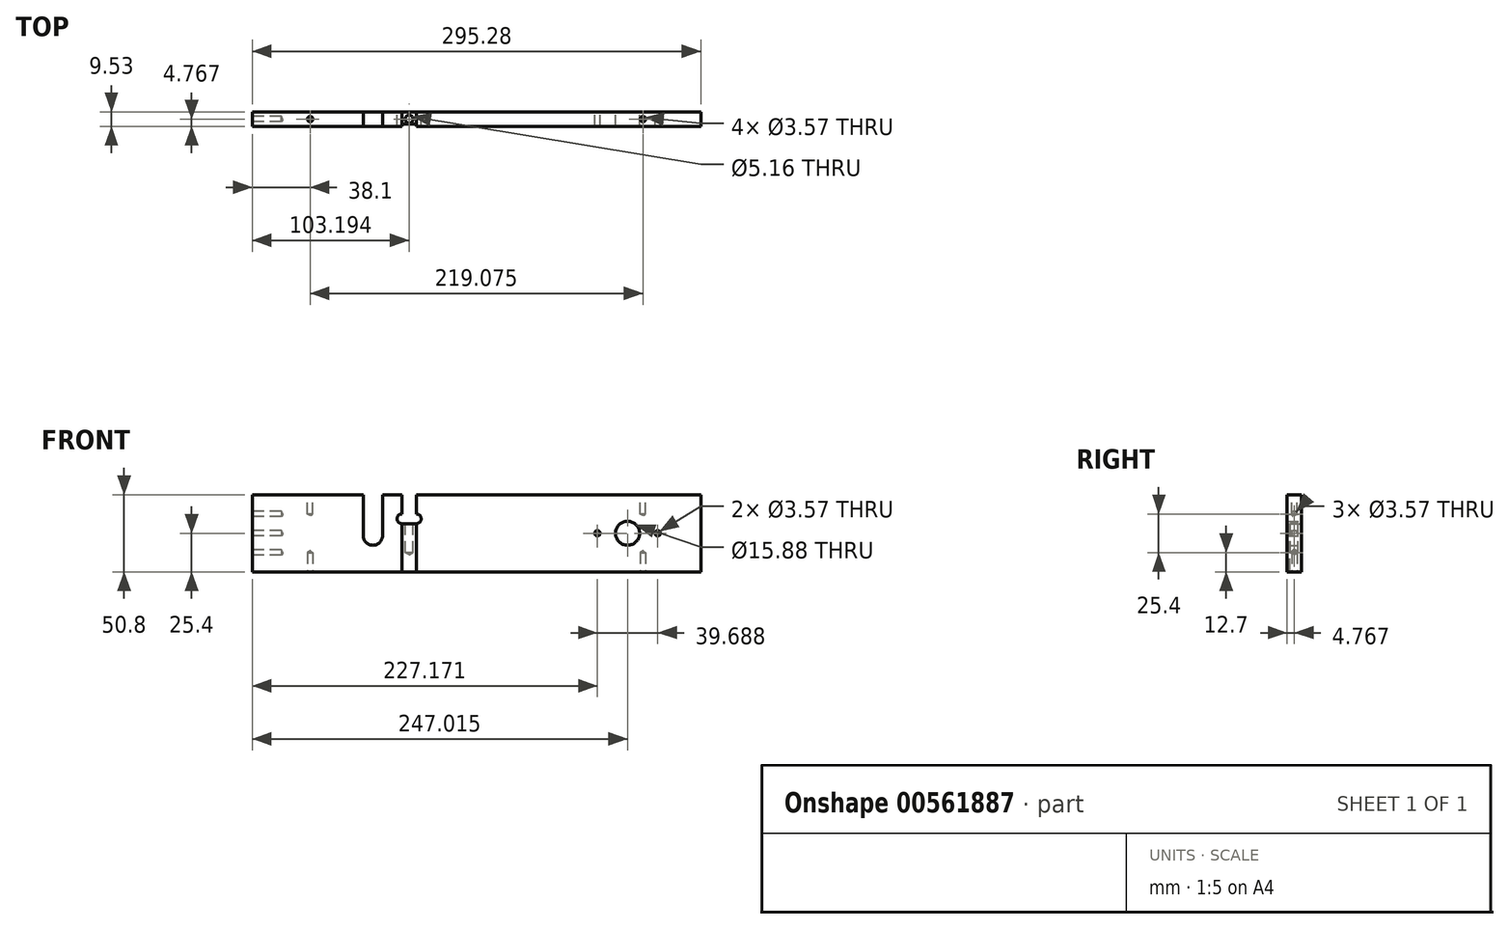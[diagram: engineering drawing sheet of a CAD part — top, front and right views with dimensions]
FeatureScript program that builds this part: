
annotation { "Feature Type Name" : "Feature", "Feature Type Description" : "" }
export const myFeature = defineFeature(function(context is Context, id is Id, definition is map)
    precondition{}
    {
        {
            var Q0;
            Q0=qCreatedBy(makeId("Front.planeOp"),FACE);
            var sketch = newSketch(context, id + "F0", { "sketchPlane" : qUnion([Q0])});
            skLineSegment(sketch, "E0", {"start": v(0, 0) * mm, "end": v(295.28, 0) * mm});
            skLineSegment(sketch, "E1", {"start": v(295.28, 0) * mm, "end": v(295.28, 50.8) * mm});
            skLineSegment(sketch, "E2", {"start": v(0, 50.8) * mm, "end": v(0, 0) * mm});
            skLineSegment(sketch, "E3", {"start": v(0, 50.8) * mm, "end": v(98.43, 50.8) * mm});
            skLineSegment(sketch, "E4", {"start": v(98.43, 50.8) * mm, "end": v(98.43, 31.75) * mm});
            skLineSegment(sketch, "E5", {"start": v(107.96, 50.8) * mm, "end": v(107.96, 31.75) * mm});
            skLineSegment(sketch, "E6", {"start": v(98.43, 31.75) * mm, "end": v(107.96, 31.75) * mm});
            skLineSegment(sketch, "E7", {"start": v(107.96, 50.8) * mm, "end": v(295.28, 50.8) * mm});
            skLineSegment(sketch, "E8", {"start": v(79.38, 50.8) * mm, "end": v(79.38, 0) * mm, "construction": true});
            skArc(sketch, "E9", {"start": v(98.42, 38.1) * mm, "mid": v(95.25, 34.92) * mm, "end": v(98.43, 31.75) * mm});
            skArc(sketch, "E10", {"start": v(107.96, 31.75) * mm, "mid": v(111.14, 34.92) * mm, "end": v(107.96, 38.1) * mm});
            skCircle(sketch, "E11", {"center": v(79.38, 25.4) * mm, "radius": 38.1 * mm, "construction": true});
            skCircle(sketch, "E12", {"center": v(79.38, 23.81) * mm, "radius": 6.35 * mm});
            skLineSegment(sketch, "E13", {"start": v(73.03, 50.8) * mm, "end": v(73.03, 23.81) * mm});
            skLineSegment(sketch, "E14", {"start": v(85.72, 50.8) * mm, "end": v(85.72, 23.81) * mm});
            skCircle(sketch, "E15", {"center": v(247.02, 25.4) * mm, "radius": 38.1 * mm, "construction": true});
            skCircle(sketch, "E16", {"center": v(247.02, 25.4) * mm, "radius": 7.94 * mm});
            skLineSegment(sketch, "E17", {"start": v(247.02, 50.8) * mm, "end": v(247.02, 0) * mm, "construction": true});
            skCircle(sketch, "E18", {"center": v(227.17, 25.4) * mm, "radius": 1.79 * mm});
            skCircle(sketch, "E19", {"center": v(266.86, 25.4) * mm, "radius": 1.79 * mm});
            skLineSegment(sketch, "E20", {"start": v(227.17, 25.4) * mm, "end": v(247.02, 25.4) * mm, "construction": true});
            skLineSegment(sketch, "E21", {"start": v(266.86, 25.4) * mm, "end": v(247.02, 25.4) * mm, "construction": true});
            skSolve(sketch);
        }
        {
            var Q0;
            Q0=makeQuery(id+"F0.imprint","IMPRINT",FACE,{"disambiguationData":[TD([[makeQuery(id+"F0.imprint","IMPRINT",EDGE,{"derivedFrom":sQuery(id+"F0.wireOp",EDGE,"E0")}),1.0]])]});
            extrude(context, id + "F1", {"entities" : qUnion([Q0]), "depth" : 9.52 * mm, "offsetDistance" : 25.4 * mm});
        }
        {
            var Q0;
            Q0=makeQuery(id+"F1.opExtrude","CAP_FACE",FACE,{"disambiguationData":[OSD([sQuery(id+"F0.wireOp",EDGE,"E0"),sQuery(id+"F0.wireOp",EDGE,"E1"),sQuery(id+"F0.wireOp",EDGE,"E2"),sQuery(id+"F0.wireOp",EDGE,"E3"),sQuery(id+"F0.wireOp",EDGE,"E4"),sQuery(id+"F0.wireOp",EDGE,"E5"),sQuery(id+"F0.wireOp",EDGE,"E6"),sQuery(id+"F0.wireOp",EDGE,"E7")])],"isStart":false});
            var sketch = newSketch(context, id + "F2", { "sketchPlane" : qUnion([Q0])});
            skLineSegment(sketch, "E22.bottom", {"start": v(107.96, 31.75) * mm, "end": v(98.43, 31.75) * mm});
            skLineSegment(sketch, "E22.top", {"start": v(107.96, 0) * mm, "end": v(98.43, 0) * mm});
            skLineSegment(sketch, "E22.left", {"start": v(107.96, 31.75) * mm, "end": v(107.96, 0) * mm});
            skLineSegment(sketch, "E22.right", {"start": v(98.43, 31.75) * mm, "end": v(98.43, 0) * mm});
            skSolve(sketch);
        }
        {
            var Q0;
            Q0=makeQuery(id+"F2.imprint","IMPRINT",FACE,{"disambiguationData":[TD([[makeQuery(id+"F2.imprint","IMPRINT",EDGE,{"derivedFrom":sQuery(id+"F2.wireOp",EDGE,"E22.bottom")}),-1.0]])]});
            extrude(context, id + "F3", {"entities" : qUnion([Q0]), "operationType" : NewBodyOperationType.REMOVE, "oppositeDirection" : true, "depth" : 1.59 * mm, "offsetDistance" : 25.4 * mm});
        }
        {
            var Q0;
            Q0=makeQuery(id+"F1.opExtrude","SWEPT_FACE",FACE,{"disambiguationData":[OSD([sQuery(id+"F0.wireOp",EDGE,"E2")])]});
            var sketch = newSketch(context, id + "F4", { "sketchPlane" : qUnion([Q0])});
            skLineSegment(sketch, "E23", {"start": v(4.76, 50.8) * mm, "end": v(4.76, 0) * mm, "construction": true});
            skLineSegment(sketch, "E24", {"start": v(0, 25.4) * mm, "end": v(9.53, 25.4) * mm, "construction": true});
            skPoint(sketch, "E25", {"position": v(4.76, 25.4) * mm});
            skPoint(sketch, "E26", {"position": v(4.76, 38.1) * mm});
            skPoint(sketch, "E27", {"position": v(4.76, 12.7) * mm});
            skSolve(sketch);
        }
        {
            var Q0;
            Q0=sQuery(id+"F4.wireOp",VERTEX,"E26");
            var Q1;
            Q1=sQuery(id+"F4.wireOp",VERTEX,"E25");
            var Q2;
            Q2=sQuery(id+"F4.wireOp",VERTEX,"E27");
            var Q3;
            Q3=makeQuery(id+"F1.opExtrude","SWEPT_BODY",BODY,{"disambiguationData":[OSD([sQuery(id+"F0.wireOp",EDGE,"E0"),sQuery(id+"F0.wireOp",EDGE,"E1"),sQuery(id+"F0.wireOp",EDGE,"E2"),sQuery(id+"F0.wireOp",EDGE,"E3"),sQuery(id+"F0.wireOp",EDGE,"E4"),sQuery(id+"F0.wireOp",EDGE,"E5"),sQuery(id+"F0.wireOp",EDGE,"E6"),sQuery(id+"F0.wireOp",EDGE,"E7"),sQuery(id+"F0.wireOp",EDGE,"E9"),sQuery(id+"F0.wireOp",EDGE,"E10"),sQuery(id+"F0.wireOp",EDGE,"E12"),sQuery(id+"F0.wireOp",EDGE,"E13"),sQuery(id+"F0.wireOp",EDGE,"E14"),sQuery(id+"F0.wireOp",EDGE,"E16")])]});
            hole(context, id + "F5", {"style" : HoleStyle.SIMPLE, "endStyle" : HoleEndStyle.BLIND, "holeDiameter" : 3.57 * mm, "majorDiameter" : 6.35 * mm, "holeDepth" : 19.05 * mm, "isTappedThrough" : true, "tappedDepth" : 12.7 * mm, "tapClearance" : 3, "startFromSketch" : true, "locations" : qUnion([Q0, Q1, Q2]), "scope" : qUnion([Q3])});
        }
        {
            var Q0;
            Q0=makeQuery(id+"F1.opExtrude","SWEPT_FACE",FACE,{"disambiguationData":[OSD([sQuery(id+"F0.wireOp",EDGE,"E6")])]});
            var sketch = newSketch(context, id + "F6", { "sketchPlane" : qUnion([Q0])});
            skLineSegment(sketch, "E28.bottom", {"start": v(98.43, 0) * mm, "end": v(107.96, 0) * mm, "construction": true});
            skLineSegment(sketch, "E28.top", {"start": v(98.43, -9.52) * mm, "end": v(107.96, -9.52) * mm, "construction": true});
            skLineSegment(sketch, "E28.left", {"start": v(98.43, 0) * mm, "end": v(98.43, -9.53) * mm, "construction": true});
            skLineSegment(sketch, "E28.right", {"start": v(107.96, 0) * mm, "end": v(107.96, -9.53) * mm, "construction": true});
            skLineSegment(sketch, "E29", {"start": v(98.43, -9.52) * mm, "end": v(107.96, 0) * mm, "construction": true});
            skLineSegment(sketch, "E30", {"start": v(98.43, 0) * mm, "end": v(107.96, -9.53) * mm, "construction": true});
            skPoint(sketch, "E31", {"position": v(103.2, -4.76) * mm});
            skSolve(sketch);
        }
        {
            var Q0;
            Q0=sQuery(id+"F6.wireOp",VERTEX,"E31");
            var Q1;
            Q1=makeQuery(id+"F1.opExtrude","SWEPT_BODY",BODY,{"disambiguationData":[OSD([sQuery(id+"F0.wireOp",EDGE,"E0"),sQuery(id+"F0.wireOp",EDGE,"E1"),sQuery(id+"F0.wireOp",EDGE,"E2"),sQuery(id+"F0.wireOp",EDGE,"E3"),sQuery(id+"F0.wireOp",EDGE,"E4"),sQuery(id+"F0.wireOp",EDGE,"E5"),sQuery(id+"F0.wireOp",EDGE,"E6"),sQuery(id+"F0.wireOp",EDGE,"E7"),sQuery(id+"F0.wireOp",EDGE,"E9"),sQuery(id+"F0.wireOp",EDGE,"E10"),sQuery(id+"F0.wireOp",EDGE,"E12"),sQuery(id+"F0.wireOp",EDGE,"E13"),sQuery(id+"F0.wireOp",EDGE,"E14"),sQuery(id+"F0.wireOp",EDGE,"E16")])]});
            hole(context, id + "F7", {"style" : HoleStyle.SIMPLE, "endStyle" : HoleEndStyle.BLIND, "holeDiameter" : 5.16 * mm, "majorDiameter" : 6.35 * mm, "holeDepth" : 19.05 * mm, "isTappedThrough" : true, "tappedDepth" : 12.7 * mm, "tapClearance" : 3, "startFromSketch" : true, "locations" : qUnion([Q0]), "scope" : qUnion([Q1])});
        }
        {
            var Q0;
            {var subQ0=sQuery(id+"F0.wireOp",EDGE,"E3");Q0=makeQuery(id+"F1.opExtrude","SWEPT_FACE",FACE,{"disambiguationData":[OSD([subQ0]),TDD([makeQuery(id+"F0.imprint","IMPRINT",EDGE,{"disambiguationData":[TD([[makeQuery(id+"F0.imprint","INTERSECT",VERTEX,{"derivedFrom":[sQuery(id+"F0.wireOp",EDGE,"E2"),subQ0]}),-1.0]])],"derivedFrom":subQ0})])]});}
            var sketch = newSketch(context, id + "F8", { "sketchPlane" : qUnion([Q0])});
            skLineSegment(sketch, "E32", {"start": v(0, -4.76) * mm, "end": v(38.1, -4.76) * mm, "construction": true});
            skPoint(sketch, "E33", {"position": v(38.1, -4.76) * mm});
            skSolve(sketch);
        }
        {
            var Q0;
            Q0=makeQuery(id+"F1.opExtrude","SWEPT_FACE",FACE,{"disambiguationData":[OSD([sQuery(id+"F0.wireOp",EDGE,"E7")])]});
            var sketch = newSketch(context, id + "F9", { "sketchPlane" : qUnion([Q0])});
            skLineSegment(sketch, "E34", {"start": v(295.28, -4.76) * mm, "end": v(257.18, -4.76) * mm, "construction": true});
            skPoint(sketch, "E35", {"position": v(257.18, -4.76) * mm});
            skSolve(sketch);
        }
        {
            var Q0;
            Q0=makeQuery(id+"F1.opExtrude","SWEPT_FACE",FACE,{"disambiguationData":[OSD([sQuery(id+"F0.wireOp",EDGE,"E0")])]});
            var sketch = newSketch(context, id + "F10", { "sketchPlane" : qUnion([Q0])});
            skLineSegment(sketch, "E36", {"start": v(0, 4.76) * mm, "end": v(38.1, 4.76) * mm, "construction": true});
            skLineSegment(sketch, "E37", {"start": v(295.28, 4.76) * mm, "end": v(257.18, 4.76) * mm, "construction": true});
            skPoint(sketch, "E38", {"position": v(257.18, 4.76) * mm});
            skPoint(sketch, "E39", {"position": v(38.1, 4.76) * mm});
            skPoint(sketch, "E40", {"position": v(33.46, 25.14) * mm});
            skSolve(sketch);
        }
        {
            var Q0;
            Q0=sQuery(id+"F10.wireOp",VERTEX,"E39");
            var Q1;
            Q1=sQuery(id+"F8.wireOp",VERTEX,"E33");
            var Q2;
            Q2=sQuery(id+"F9.wireOp",VERTEX,"E35");
            var Q3;
            Q3=sQuery(id+"F10.wireOp",VERTEX,"E38");
            var Q4;
            Q4=makeQuery(id+"F1.opExtrude","SWEPT_BODY",BODY,{"disambiguationData":[OSD([sQuery(id+"F0.wireOp",EDGE,"E0"),sQuery(id+"F0.wireOp",EDGE,"E1"),sQuery(id+"F0.wireOp",EDGE,"E2"),sQuery(id+"F0.wireOp",EDGE,"E3"),sQuery(id+"F0.wireOp",EDGE,"E4"),sQuery(id+"F0.wireOp",EDGE,"E5"),sQuery(id+"F0.wireOp",EDGE,"E6"),sQuery(id+"F0.wireOp",EDGE,"E7"),sQuery(id+"F0.wireOp",EDGE,"E9"),sQuery(id+"F0.wireOp",EDGE,"E10"),sQuery(id+"F0.wireOp",EDGE,"E12"),sQuery(id+"F0.wireOp",EDGE,"E13"),sQuery(id+"F0.wireOp",EDGE,"E14"),sQuery(id+"F0.wireOp",EDGE,"E16")])]});
            hole(context, id + "F11", {"style" : HoleStyle.SIMPLE, "endStyle" : HoleEndStyle.BLIND, "holeDiameter" : 3.57 * mm, "majorDiameter" : 6.35 * mm, "holeDepth" : 12.7 * mm, "isTappedThrough" : true, "tappedDepth" : 12.7 * mm, "tapClearance" : 3, "startFromSketch" : true, "locations" : qUnion([Q0, Q1, Q2, Q3]), "scope" : qUnion([Q4])});
        }
    });
